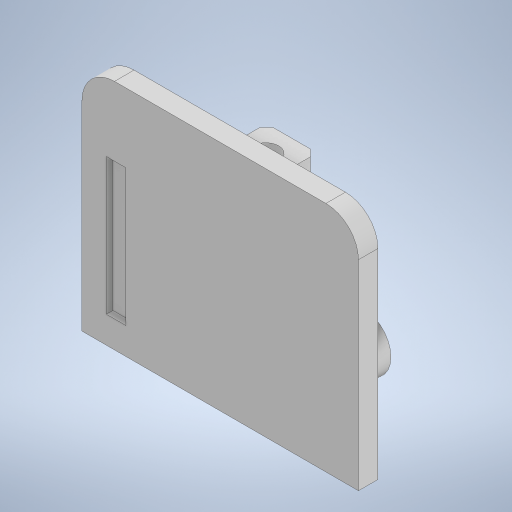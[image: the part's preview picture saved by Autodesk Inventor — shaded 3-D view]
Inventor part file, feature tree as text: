
AUTODESK INVENTOR PART (.ipt)
format: ipt  version: 2023 (Build 270158000, 158)  size: 324,608 bytes
history: native  units: mm
features: extrude x7, sketch x7, other x2, pattern_linear x2, chamfer x2, projected_geometry x2, fillet x1
ambient origin geometry x8: Origin, YZ Plane, XZ Plane, XY Plane, X Axis, Y Axis, Z Axis, Center Point
bodies: Body1 (feature_tree)
feature tree (23):
  other  "솔리드1"
  extrude  "돌출1"  Depth=42.5mm
  fillet  "모깎기1"  Radius=36.25mm
  other  "작업 평면1"
  extrude  "돌출2"  Depth=3.0mm TaperAngle=0.0deg
  pattern_linear  "직사각형 패턴1"  Spacing1=5.0mm  [1 undecoded]
  extrude  "돌출3"  [1 undecoded]
  extrude  "돌출4"  Depth=4.0mm
  extrude  "돌출5"  Depth=4.0mm
  chamfer  "모따기1"  Distance=8.0mm
  extrude  "돌출6"  Depth=10.0mm
  extrude  "돌출7"  Depth=2.0mm TaperAngle=0.0deg
  pattern_linear  "직사각형 패턴2"  Count1=2 Spacing1=22.5mm
  chamfer  "모따기2"  Distance=15.8mm
  sketch  "스케치1"
  sketch  "스케치2"
  sketch  "스케치3"
  sketch  "스케치4"
  sketch  "스케치5"
  sketch  "스케치6"
  projected_geometry  "투영된 루프1"
  projected_geometry  "투영된 루프2"
  sketch  "스케치7"
note: 2 required parameter values undecoded (feature->parameter linkage not recoverable at this tier; creation-order binding heuristic only, values carry confidence <= 0.55)
